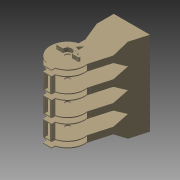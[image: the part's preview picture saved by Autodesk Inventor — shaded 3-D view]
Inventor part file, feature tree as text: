
AUTODESK INVENTOR PART (.ipt)
format: ipt  version: 2015 (Build 190159000, 159)  size: 483,328 bytes
history: native  units: mm
features: extrude x16, sketch x16, thread x12, pattern_linear x9, chamfer x2, shell x1
ambient origin geometry x8: Origin, YZ Plane, XZ Plane, XY Plane, X Axis, Y Axis, Z Axis, Center Point
bodies: 实体1 (feature_tree)
feature tree (56):
  extrude  "拉伸1"  Depth=30.0mm
  extrude  "拉伸2"  Depth=300.0mm
  shell  "抽壳1"  Thickness=25.0mm
  extrude  "拉伸3"  Depth=490.0mm TaperAngle=0.0deg
  pattern_linear  "矩形阵列1"  Count1=12  [1 undecoded]
  pattern_linear  "矩形阵列2"  Count1=9  [1 undecoded]
  extrude  "拉伸4"  Depth=5.0mm
  extrude  "拉伸5"  Depth=33.0mm
  pattern_linear  "矩形阵列3"  Count1=4  [1 undecoded]
  extrude  "拉伸6"  Depth=30.0mm
  extrude  "拉伸7"  Depth=5.0mm TaperAngle=0.0deg
  pattern_linear  "矩形阵列4"  Spacing1=8.0mm  [1 undecoded]
  extrude  "拉伸8"  Depth=10.0mm
  pattern_linear  "矩形阵列5"  Spacing1=5.0mm  [1 undecoded]
  extrude  "拉伸9"  Depth=40.0mm
  thread  "螺纹5"  [1 undecoded]
  thread  "螺纹6"  [1 undecoded]
  thread  "螺纹7"  [1 undecoded]
  thread  "螺纹8"  [1 undecoded]
  pattern_linear  "矩形阵列7"  Count1=4  [1 undecoded]
  extrude  "拉伸10"  Depth=10.0mm
  thread  "螺纹9"  [1 undecoded]
  thread  "螺纹10"  [1 undecoded]
  pattern_linear  "矩形阵列8"  Count1=3  [1 undecoded]
  extrude  "拉伸11"  Depth=5.0mm
  thread  "螺纹11"  [1 undecoded]
  thread  "螺纹12"  [1 undecoded]
  pattern_linear  "矩形阵列9"  Spacing1=10.0mm  [1 undecoded]
  extrude  "拉伸12"  Depth=10.0mm
  extrude  "拉伸13"  Depth=10.0mm
  extrude  "拉伸14"  Depth=5.0mm TaperAngle=0.0deg
  pattern_linear  "矩形阵列10"  Spacing1=10.0mm  [1 undecoded]
  chamfer  "倒角1"  Distance=10.0mm
  chamfer  "倒角2"  Distance=10.0mm
  extrude  "拉伸15"  Depth=10.0mm TaperAngle=0.0deg
  thread  "螺纹13"  [1 undecoded]
  thread  "螺纹14"  [1 undecoded]
  extrude  "拉伸16"  Depth=5.0mm
  thread  "螺纹15"  [1 undecoded]
  thread  "螺纹16"  [1 undecoded]
  sketch  "草图1"  dims[d0=200.0mm d2=30.0mm]
  sketch  "草图3"  dims[d3=300.0mm d5=205.0mm d6=25.0mm]
  sketch  "草图4"  dims[d7=5.0mm d8=490.0mm d9=0.0mm]
  sketch  "草图5"  dims[d15=46.0mm]
  sketch  "草图6"  dims[d16=38.0mm]
  sketch  "草图7"  dims[d17=82.0mm]
  sketch  "草图8"  dims[d18=38.0mm]
  sketch  "草图9"  dims[d19=82.0mm]
  sketch  "草图10"  dims[d20=38.0mm]
  sketch  "草图11"  dims[d21=82.0mm]
  sketch  "草图12"  dims[d22=38.0mm]
  sketch  "草图13"  dims[d23=46.0mm d25=120.0mm]
  sketch  "草图14"  dims[d26=5.0mm]
  sketch  "草图15"  dims[d27=5.0mm d28=90.0mm]
  sketch  "草图16"  dims[d29=200.0mm d30=0.0mm d31=5.0mm]
  sketch  "草图17"  dims[d32=5.0mm d33=0.0mm d34=20.0mm d36=33.0mm d37=40.0mm d39=120.0mm d40=30.0mm d41=5.0mm d42=0.0mm d43=8.0mm d44=2.2mm d45=5.0mm d46=0.0mm d47=40.0mm d49=120.0mm d50=50.0mm d51=18.0mm d52=38.0mm d53=0.0mm d54=5.0mm d55=0.0mm d56=40.0mm d58=120.0mm d59=10.0mm d60=10.0mm d61=5.0mm d62=0.0mm d63=30.0mm d65=120.0mm d66=5.0mm d67=5.0mm d68=10.0mm d69=10.0mm d70=20.0mm d71=20.0mm d72=5.0mm d73=0.0mm d85=10.0mm d86=0.0mm d87=10.0mm d88=0.0mm d89=10.0mm d90=0.0mm d91=10.0mm d92=0.0mm d93=30.0mm d95=120.0mm d96=5.0mm d97=5.0mm d98=8.0mm d99=8.0mm d100=230.57mm d101=230.57mm d102=5.0mm d103=0.0mm d104=10.0mm d105=0.0mm d106=10.0mm d107=0.0mm d108=40.0mm d110=120.0mm d111=5.0mm d112=5.0mm d113=8.0mm d114=8.0mm d115=15.0mm d116=15.0mm d117=5.0mm d118=0.0mm d119=10.0mm d120=0.0mm d121=10.0mm d122=0.0mm d123=40.0mm d125=120.0mm d126=45.0mm d127=26.0mm d128=10.0mm d129=10.0mm d130=8.65257mm d131=130.0mm d132=23.0mm d133=0.0mm d134=8.0mm d135=10.0mm d136=11.5mm d137=8.0mm d138=110.0mm d139=11.5mm d140=30.0mm d141=0.0mm d142=6.0mm d143=50.0mm d144=23.0mm d145=0.0mm d146=20.0mm d148=421.0mm d149=50.0mm d150=23.0mm d151=45.0deg d152=50.0mm d153=23.0mm d154=45.0deg d155=5.0mm d156=5.0mm d157=35.5mm d158=13.141315mm d159=45.0deg d160=23.0mm d161=0.0mm d162=10.0mm d163=0.0mm d164=10.0mm d165=0.0mm d166=5.0mm d167=5.0mm d168=23.0mm d169=0.0mm d170=10.0mm d171=0.0mm d172=10.0mm d173=0.0mm d174=35.5mm]
note: 21 required parameter values undecoded (feature->parameter linkage not recoverable at this tier; creation-order binding heuristic only, values carry confidence <= 0.55)
